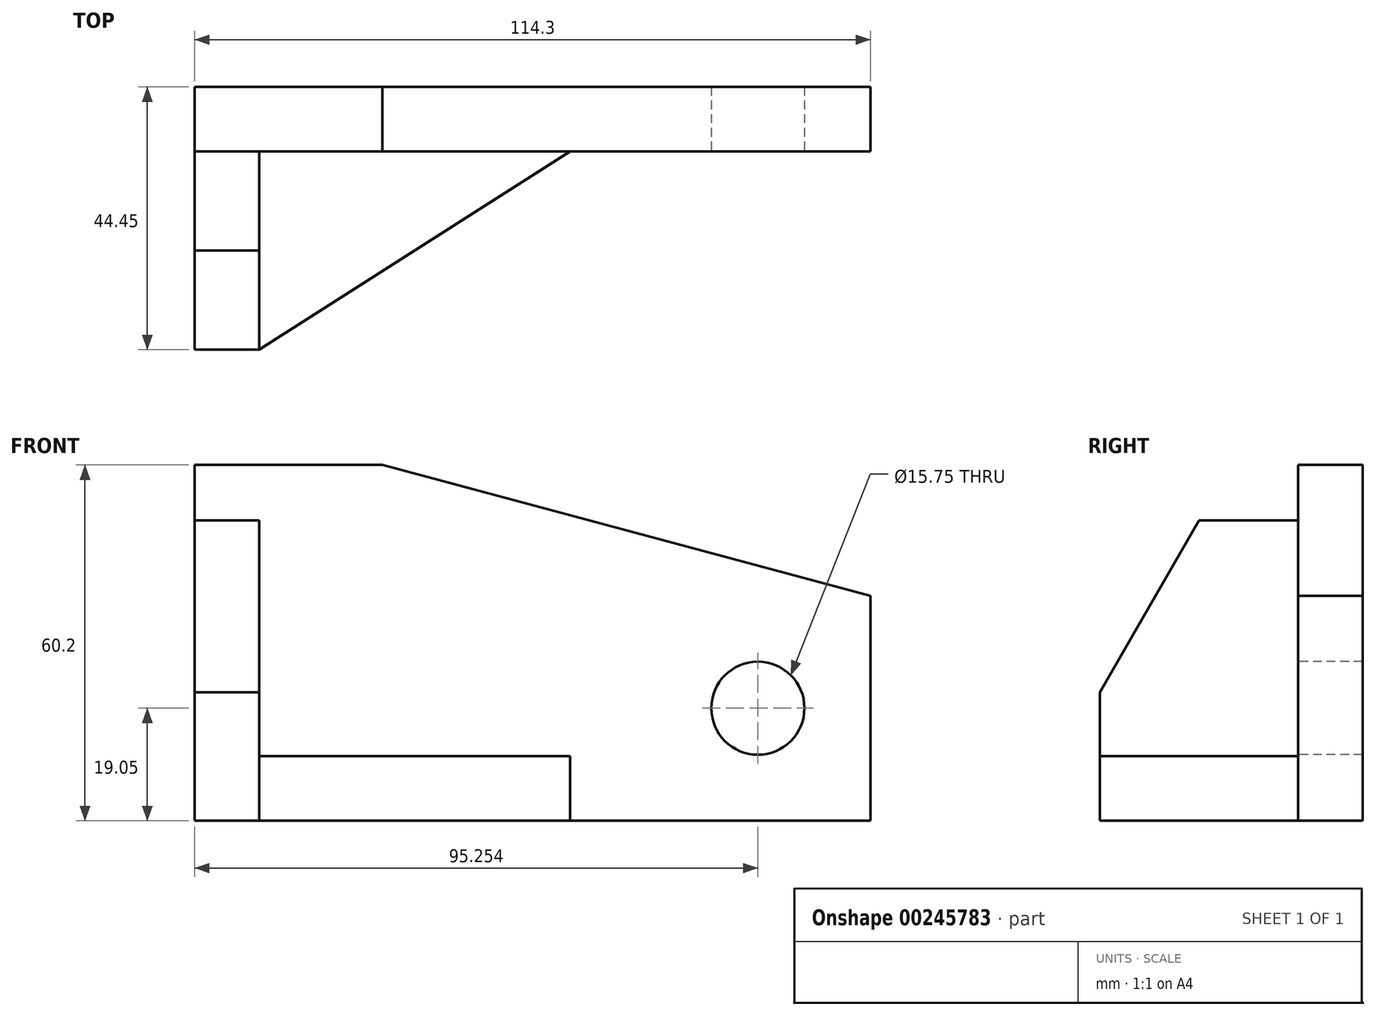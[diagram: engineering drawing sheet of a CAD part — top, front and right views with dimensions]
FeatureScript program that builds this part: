
annotation { "Feature Type Name" : "Feature", "Feature Type Description" : "" }
export const myFeature = defineFeature(function(context is Context, id is Id, definition is map)
    precondition{}
    {
        {
            var Q0;
            Q0=qCreatedBy(makeId("Top.planeOp"),FACE);
            var sketch = newSketch(context, id + "F0", { "sketchPlane" : qUnion([Q0])});
            skLineSegment(sketch, "E0", {"start": v(-55.45, 21.55) * mm, "end": v(-55.45, -22.9) * mm});
            skLineSegment(sketch, "E1", {"start": v(8.05, 10.63) * mm, "end": v(58.85, 10.63) * mm});
            skLineSegment(sketch, "E2", {"start": v(58.85, 10.63) * mm, "end": v(58.85, 21.55) * mm});
            skLineSegment(sketch, "E3", {"start": v(58.85, 21.55) * mm, "end": v(-55.45, 21.55) * mm});
            skLineSegment(sketch, "E4", {"start": v(-55.45, -22.9) * mm, "end": v(-44.52, -22.9) * mm});
            skLineSegment(sketch, "E5", {"start": v(-44.52, -22.9) * mm, "end": v(8.05, 10.63) * mm});
            skSolve(sketch);
        }
        {
            var Q0;
            Q0=makeQuery(id+"F0.imprint","IMPRINT",FACE,{"disambiguationData":[TD([[makeQuery(id+"F0.imprint","IMPRINT",EDGE,{"derivedFrom":sQuery(id+"F0.wireOp",EDGE,"E0")}),1.0]])]});
            extrude(context, id + "F1", {"entities" : qUnion([Q0]), "depth" : 60.2 * mm});
        }
        {
            var Q0;
            Q0=makeQuery(id+"F1.opExtrude","CAP_FACE",FACE,{"disambiguationData":[OSD([sQuery(id+"F0.wireOp",EDGE,"E0"),sQuery(id+"F0.wireOp",EDGE,"E1"),sQuery(id+"F0.wireOp",EDGE,"E2"),sQuery(id+"F0.wireOp",EDGE,"E3"),sQuery(id+"F0.wireOp",EDGE,"E4"),sQuery(id+"F0.wireOp",EDGE,"E5")])],"isStart":false});
            var sketch = newSketch(context, id + "F2", { "sketchPlane" : qUnion([Q0])});
            skLineSegment(sketch, "E6", {"start": v(-44.52, -22.9) * mm, "end": v(-44.52, 10.63) * mm});
            skLineSegment(sketch, "E7", {"start": v(-44.52, 10.63) * mm, "end": v(8.05, 10.63) * mm});
            skSolve(sketch);
        }
        {
            var Q0;
            Q0=makeQuery(id+"F2.imprint","IMPRINT",FACE,{"disambiguationData":[TD([[makeQuery(id+"F2.imprint","IMPRINT",EDGE,{"derivedFrom":sQuery(id+"F2.wireOp",EDGE,"E6")}),-1.0]])]});
            extrude(context, id + "F3", {"entities" : qUnion([Q0]), "operationType" : NewBodyOperationType.REMOVE, "oppositeDirection" : true, "depth" : 49.28 * mm});
        }
        {
            var Q0;
            Q0=makeQuery(id+"F3.boolean.opBoolean","COPY",FACE,{"derivedFrom":makeQuery(id+"F3.opExtrude","SWEPT_FACE",FACE,{"disambiguationData":[OSD([sQuery(id+"F2.wireOp",EDGE,"E6")])]})});
            var sketch = newSketch(context, id + "F4", { "sketchPlane" : qUnion([Q0])});
            skLineSegment(sketch, "E8", {"start": v(-22.9, 10.92) * mm, "end": v(-22.9, 21.76) * mm});
            skLineSegment(sketch, "E9", {"start": v(-22.9, 21.76) * mm, "end": v(-6.13, 50.8) * mm});
            skPoint(sketch, "E9.endSnap0", {"position": v(-6.13, 60.2) * mm});
            skLineSegment(sketch, "E10", {"start": v(-6.13, 50.8) * mm, "end": v(10.63, 50.8) * mm});
            skSolve(sketch);
        }
        {
            var Q0;
            {var subQ2=sQuery(id+"F4.wireOp",EDGE,"E9");Q0=makeQuery(id+"F4.imprint","IMPRINT",FACE,{"disambiguationData":[TD([[makeQuery(id+"F4.imprint","IMPRINT",EDGE,{"derivedFrom":subQ2}),1.0]])]});}
            extrude(context, id + "F5", {"entities" : qUnion([Q0]), "operationType" : NewBodyOperationType.REMOVE, "oppositeDirection" : true, "depth" : 10.92 * mm});
        }
        {
            var Q0;
            {var subQ0=sQuery(id+"F2.wireOp",EDGE,"E7");Q0=makeQuery(id+"F5.boolean.opBoolean","MERGE",FACE,{"derivedFrom":[makeQuery(id+"F3.boolean.opBoolean","MERGE",FACE,{"derivedFrom":[makeQuery(id+"F1.opExtrude","SWEPT_FACE",FACE,{"disambiguationData":[OSD([sQuery(id+"F0.wireOp",EDGE,"E1")])]}),makeQuery(id+"F3.opExtrude","SWEPT_FACE",FACE,{"disambiguationData":[OSD([subQ0])]})]}),makeQuery(id+"F5.opExtrude","SWEPT_FACE",FACE,{"disambiguationData":[OSD([sQuery(id+"F2.wireOp",EDGE,"E6"),subQ0])]})]});}
            var sketch = newSketch(context, id + "F6", { "sketchPlane" : qUnion([Q0])});
            skLineSegment(sketch, "E11", {"start": v(-23.7, 60.2) * mm, "end": v(58.85, 38.08) * mm});
            skCircle(sketch, "E12", {"center": v(39.8, 19.05) * mm, "radius": 7.87 * mm});
            skSolve(sketch);
        }
        {
            var Q0;
            {var subQ0=sQuery(id+"F6.wireOp",EDGE,"E11");Q0=makeQuery(id+"F6.imprint","IMPRINT",FACE,{"disambiguationData":[TD([[makeQuery(id+"F6.imprint","IMPRINT",EDGE,{"derivedFrom":subQ0}),1.0]])]});}
            var Q1;
            Q1=makeQuery(id+"F6.imprint","IMPRINT",FACE,{"disambiguationData":[TD([[makeQuery(id+"F6.imprint","IMPRINT",EDGE,{"derivedFrom":sQuery(id+"F6.wireOp",EDGE,"E12")}),1.0]])]});
            extrude(context, id + "F7", {"entities" : qUnion([Q0, Q1]), "operationType" : NewBodyOperationType.REMOVE, "oppositeDirection" : true, "depth" : 10.92 * mm});
        }
    });
